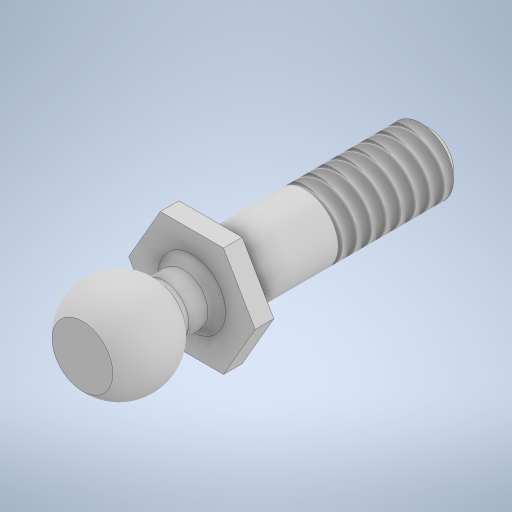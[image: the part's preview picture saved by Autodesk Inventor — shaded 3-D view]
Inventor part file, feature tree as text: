
AUTODESK INVENTOR PART (.ipt)
format: ipt  version: 2024 (Build 280153000, 153)  size: 326,144 bytes
history: native  units: in
note: dims shown in document units (in); Inventor stores cm internally (conversion verified against a paired STEP export)
features: sketch x4, extrude x3, revolve x1, fillet x1, plane x1, split x1, chamfer x1, thread x1, direct_edit x1, other x1
ambient origin geometry x8: Origin, YZ Plane, XZ Plane, XY Plane, X Axis, Y Axis, Z Axis, Center Point
bodies: Solid1 (feature_tree)
feature tree (15):
  extrude  "Extrusion1"  Depth=0.032in TaperAngle=0.0deg
  extrude  "Extrusion2"  Depth=0.125in TaperAngle=0.0deg
  revolve  "Revolution1"  Angle=90.0deg
  fillet  "Fillet1"  Radius=0.015in
  plane  "Work Plane1"
  split  "Split1"
  extrude  "Extrusion3"  Depth=0.3937in
  chamfer  "Chamfer1"  Distance=0.375in
  thread  "Thread1"  [1 undecoded]
  direct_edit  "Direct Edit1"
  sketch  "Sketch1"  dims[d0=0.1875in d1=0.032in d2=0.0in]
  sketch  "Sketch2"  dims[d3=0.085in d4=0.125in d5=0.0in]
  sketch  "Sketch3"  dims[d6=0.1625in d7=90.0deg d8=0.015in]
  sketch  "Sketch4"  dims[d9=0.1875in d10=0.112in d11=0.375in d12=0.0in d13=0.015in d14=0.125in d15=45.0deg d16=1.0236in d17=0.0in d18=3.937in d19=0.3937in d20=0.3937in]
  other  "Scale1"
note: 1 required parameter value undecoded (feature->parameter linkage not recoverable at this tier; creation-order binding heuristic only, values carry confidence <= 0.55)
